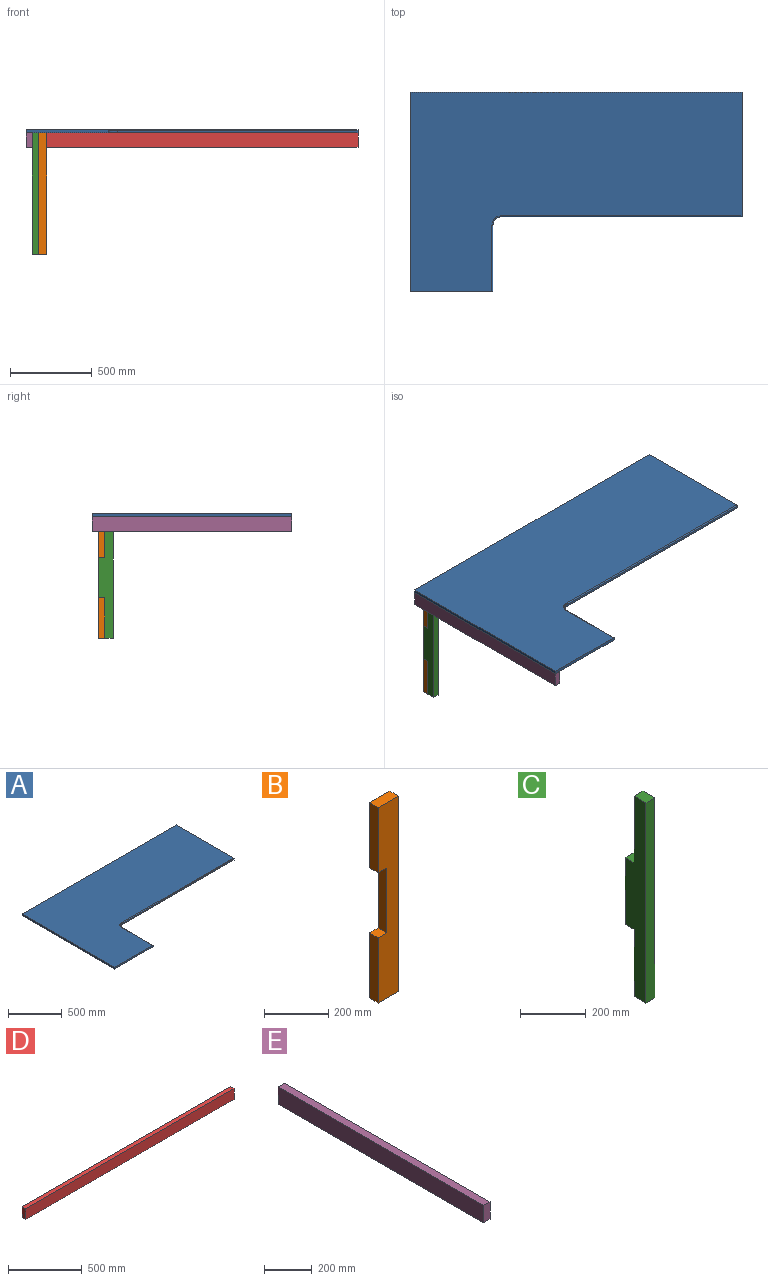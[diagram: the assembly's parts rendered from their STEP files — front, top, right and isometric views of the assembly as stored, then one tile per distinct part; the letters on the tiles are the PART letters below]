
ASSEMBLY  parts=5 mates=4
PART A: 12 faces, bbox 2032x1219.2x19.1 mm
  f0: plane 2032x19.05mm, normal (0,1,0), area 38709.6mm2, adj f1,f6,f7,f8
  f1: plane 1219.2x19.05mm, normal (-1,0,0), area 23225.8mm2, adj f0,f2,f7,f8
  f2: plane 508x19.05mm, normal (0,-1,0), area 9668.7mm2, adj f1,f3,f7,f8,f10
  f3: plane 406.4x12.7mm, normal (1,0,0), area 5161.3mm2, adj f2,f4,f7,f10
  f4: cylinder r=50.8mm len=50.8mm, axis (0,0,1), area 1013.4mm2, adj f3,f5,f7,f11
  f5: plane 1473.2x12.7mm, normal (0,-1,0), area 18709.6mm2, adj f4,f6,f7,f9
  f6: plane 762x19.05mm, normal (1,0,0), area 14507.4mm2, adj f0,f5,f7,f8,f9
  f7: plane 2032x1219.2mm, normal (0,0,-1), area 1781195.4mm2, adj f0,f1,f2,f3,f4,f5,f6
  f8: plane 2032x1219.2mm, normal (0,0,1), area 1768721.6mm2, adj f0,f1,f2,f6,f9,f10,f11
  f9: cylinder r=6.35mm len=1473.2mm, axis (1,0,0), area 14694.5mm2, adj f5,f6,f8,f11
  f10: cylinder r=6.35mm len=406.4mm, axis (0,1,0), area 4053.7mm2, adj f2,f3,f8,f11
  f11: torus R=57.15mm, axis (0,0,1), area 832.1mm2, adj f4,f8,f9,f10
PART B: 10 faces, bbox 88.9x38.1x743 mm
  f0: plane 247.65x38.1mm, normal (-1,0,0), area 9435.5mm2, adj f1,f3,f6,f8
  f1: plane 742.95x88.9mm, normal (0,-1,0), area 56612.8mm2, adj f0,f2,f4,f5,f6,f7,f8,f9
  f2: plane 247.65x38.1mm, normal (-1,0,0), area 9435.5mm2, adj f1,f3,f5,f7
  f3: plane 742.95x88.9mm, normal (0,1,0), area 56612.8mm2, adj f0,f2,f4,f5,f6,f7,f8,f9
  f4: plane 742.95x38.1mm, normal (1,0,0), area 28306.4mm2, adj f1,f3,f5,f6
  f5: plane 88.9x38.1mm, normal (0,0,-1), area 3387.1mm2, adj f1,f2,f3,f4
  f6: plane 88.9x38.1mm, normal (0,0,1), area 3387.1mm2, adj f0,f1,f3,f4
  f7: plane 38.1x38.1mm, normal (0,0,1), area 1451.6mm2, adj f1,f2,f3,f9
  f8: plane 38.1x38.1mm, normal (0,0,-1), area 1451.6mm2, adj f0,f1,f3,f9
  f9: plane 247.65x38.1mm, normal (-1,0,0), area 9435.5mm2, adj f1,f3,f7,f8
PART C: 10 faces, bbox 38.1x88.9x743 mm
  f0: plane 247.65x38.1mm, normal (0,1,0), area 9435.5mm2, adj f3,f5,f7,f9
  f1: plane 50.8x38.1mm, normal (0,0,-1), area 1935.5mm2, adj f3,f4,f5,f8
  f2: plane 50.8x38.1mm, normal (0,0,1), area 1935.5mm2, adj f3,f4,f5,f6
  f3: plane 742.95x88.9mm, normal (-1,0,0), area 47177.3mm2, adj f0,f1,f2,f4,f6,f7,f8,f9
  f4: plane 742.95x38.1mm, normal (0,-1,0), area 28306.4mm2, adj f1,f2,f3,f5
  f5: plane 742.95x88.9mm, normal (1,0,0), area 47177.3mm2, adj f0,f1,f2,f4,f6,f7,f8,f9
  f6: plane 247.65x38.1mm, normal (0,1,0), area 9435.5mm2, adj f2,f3,f5,f7
  f7: plane 38.1x38.1mm, normal (0,0,1), area 1451.6mm2, adj f0,f3,f5,f6
  f8: plane 247.65x38.1mm, normal (0,1,0), area 9435.5mm2, adj f1,f3,f5,f9
  f9: plane 38.1x38.1mm, normal (0,0,-1), area 1451.6mm2, adj f0,f3,f5,f8
PART D: 6 faces, bbox 1993.9x38.1x88.9 mm
  f0: plane 1993.9x88.9mm, normal (0,-1,0), area 177257.7mm2, adj f1,f3,f4,f5
  f1: plane 88.9x38.1mm, normal (-1,0,0), area 3387.1mm2, adj f0,f2,f4,f5
  f2: plane 1993.9x88.9mm, normal (0,1,0), area 177257.7mm2, adj f1,f3,f4,f5
  f3: plane 88.9x38.1mm, normal (1,0,0), area 3387.1mm2, adj f0,f2,f4,f5
  f4: plane 1993.9x38.1mm, normal (0,0,-1), area 75967.6mm2, adj f0,f1,f2,f3
  f5: plane 1993.9x38.1mm, normal (0,0,1), area 75967.6mm2, adj f0,f1,f2,f3
PART E: 6 faces, bbox 38.1x1219.2x88.9 mm
  f0: plane 1219.2x88.9mm, normal (1,0,0), area 108386.9mm2, adj f1,f3,f4,f5
  f1: plane 88.9x38.1mm, normal (0,-1,0), area 3387.1mm2, adj f0,f2,f4,f5
  f2: plane 1219.2x88.9mm, normal (-1,0,0), area 108386.9mm2, adj f1,f3,f4,f5
  f3: plane 88.9x38.1mm, normal (0,1,0), area 3387.1mm2, adj f0,f2,f4,f5
  f4: plane 1219.2x38.1mm, normal (0,0,-1), area 46451.5mm2, adj f0,f1,f2,f3
  f5: plane 1219.2x38.1mm, normal (0,0,1), area 46451.5mm2, adj f0,f1,f2,f3
PLACE A at identity fixed
PLACE B at identity
PLACE C at identity
PLACE D at identity
PLACE E at identity
MATE fastened C.f6 <-> B.f1  axis (0,-1,0) through (38.1,-76.2,-19.05)mm
MATE fastened B.f0 <-> D.f1  axis (1,0,0) through (38.1,-38.1,-19.05)mm
MATE fastened A.f7 <-> E.f5  axis (0,0,1) through (0,0,-19.05)mm
MATE fastened E.f0 <-> D.f1  axis (1,0,0) through (38.1,0,-19.05)mm
